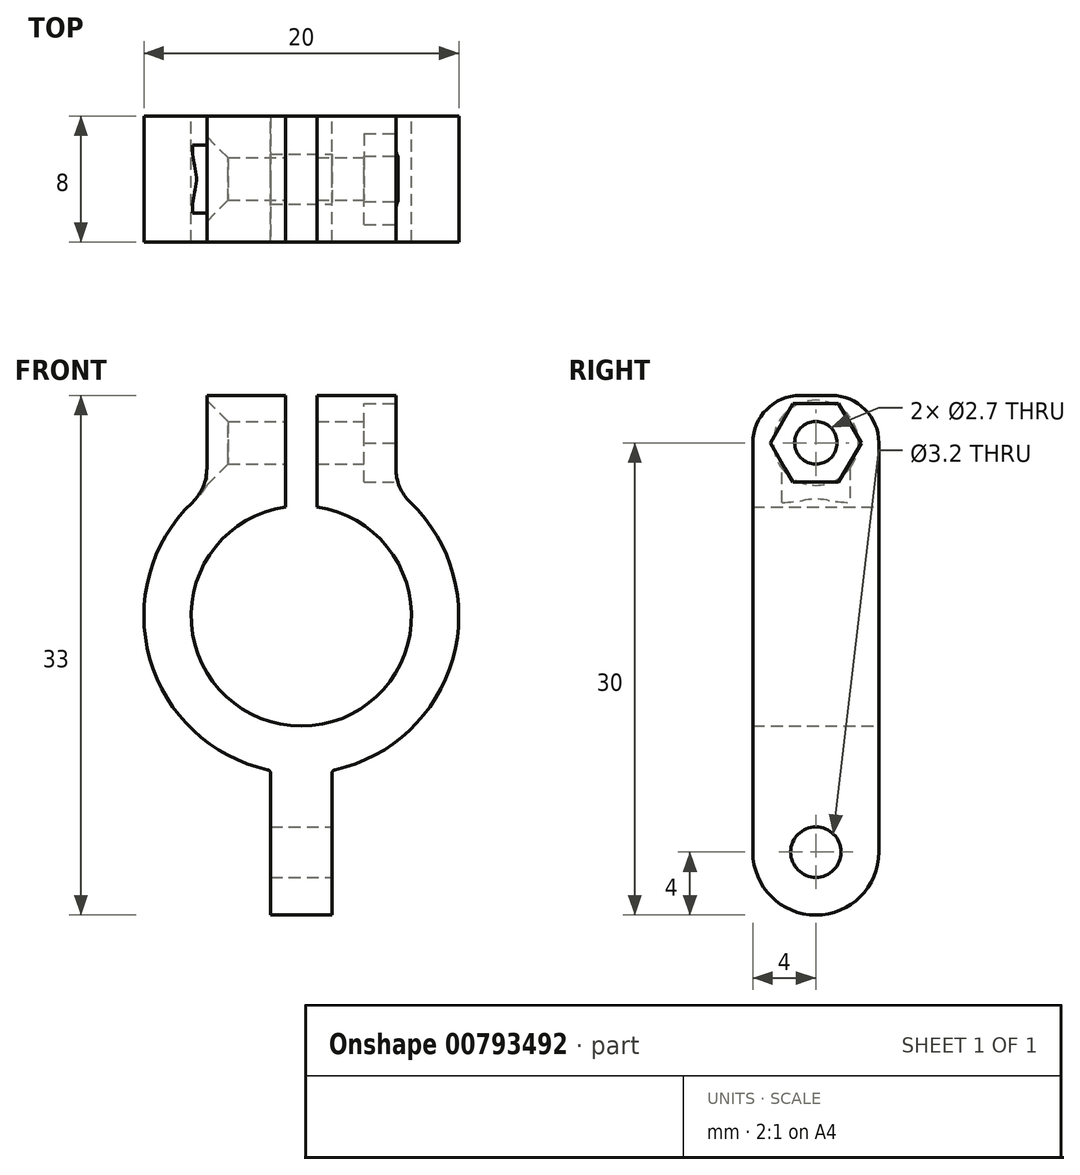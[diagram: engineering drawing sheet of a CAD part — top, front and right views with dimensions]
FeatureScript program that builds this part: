
annotation { "Feature Type Name" : "Feature", "Feature Type Description" : "" }
export const myFeature = defineFeature(function(context is Context, id is Id, definition is map)
    precondition{}
    {
        {
            var Q0;
            Q0=qCreatedBy(makeId("Front.planeOp"),FACE);
            var sketch = newSketch(context, id + "F0", { "sketchPlane" : qUnion([Q0])});
            skArc(sketch, "E0", {"start": v(-1, 6.93) * mm, "mid": v(0, -7) * mm, "end": v(1, 6.93) * mm});
            skLineSegment(sketch, "E1", {"start": v(-1, 14) * mm, "end": v(-1, 6.93) * mm});
            skLineSegment(sketch, "E2", {"start": v(1, 6.93) * mm, "end": v(1, 14) * mm});
            skLineSegment(sketch, "E3.trimOffspring", {"start": v(-1, 14) * mm, "end": v(-6, 14) * mm});
            skLineSegment(sketch, "E4", {"start": v(-1.95, -19) * mm, "end": v(-1.95, -10) * mm});
            skLineSegment(sketch, "E5", {"start": v(1.95, -10) * mm, "end": v(1.95, -19) * mm});
            skLineSegment(sketch, "E6", {"start": v(-1.95, -10) * mm, "end": v(-2.19, -10) * mm, "construction": true});
            skArc(sketch, "E7", {"start": v(-1.95, -10) * mm, "mid": v(-2, -9.85) * mm, "end": v(-2.14, -9.77) * mm});
            skLineSegment(sketch, "E8", {"start": v(-1.95, -19) * mm, "end": v(1.95, -19) * mm});
            skArc(sketch, "E9.MirrorCS", {"start": v(1.95, -10) * mm, "mid": v(2, -9.85) * mm, "end": v(2.14, -9.77) * mm});
            skLineSegment(sketch, "E10", {"start": v(-6, 14) * mm, "end": v(-6, 8) * mm});
            skArc(sketch, "E11", {"start": v(-2.14, -9.77) * mm, "mid": v(-9.77, -2.13) * mm, "end": v(-6, 8) * mm});
            skLineSegment(sketch, "E12.MirrorCS", {"start": v(6, 14) * mm, "end": v(6, 8) * mm});
            skLineSegment(sketch, "E13.MirrorCS", {"start": v(1, 14) * mm, "end": v(6, 14) * mm});
            skArc(sketch, "E14.MirrorCS", {"start": v(2.14, -9.77) * mm, "mid": v(9.77, -2.13) * mm, "end": v(6, 8) * mm});
            skSolve(sketch);
        }
        {
            var Q0;
            Q0=makeQuery(id+"F0.imprint","IMPRINT",FACE,{"disambiguationData":[TD([[makeQuery(id+"F0.imprint","IMPRINT",EDGE,{"derivedFrom":sQuery(id+"F0.wireOp",EDGE,"E0")}),-1.0]])]});
            var Q1;
            {var subQ0=sQuery(id+"F0.wireOp",EDGE,"gT4Yp9KQ-vHPQ-P8ZU-SFqX-VDEBA4EE69W3");Q1=makeQuery(id+"F0.imprint","IMPRINT",FACE,{"disambiguationData":[TD([[makeQuery(id+"F0.imprint","IMPRINT",EDGE,{"derivedFrom":subQ0}),1.0]])]});}
            extrude(context, id + "F1", {"entities" : qUnion([Q0, Q1]), "endBound" : BoundingType.SYMMETRIC, "depth" : 8 * mm, "offsetDistance" : 25 * mm});
        }
        {
            var Q0;
            Q0=makeQuery(id+"F1.opExtrude","SWEPT_FACE",FACE,{"disambiguationData":[OSD([sQuery(id+"F0.wireOp",EDGE,"E12.MirrorCS")])]});
            var sketch = newSketch(context, id + "F2", { "sketchPlane" : qUnion([Q0])});
            skCircle(sketch, "E15", {"center": v(0, 11) * mm, "radius": 1.35 * mm});
            skCircle(sketch, "E16.cCircle", {"center": v(0, 11) * mm, "radius": 2.5 * mm, "construction": true});
            skLineSegment(sketch, "E16.0", {"start": v(-1.44, 13.5) * mm, "end": v(1.44, 13.5) * mm});
            skLineSegment(sketch, "E16.1", {"start": v(1.44, 13.5) * mm, "end": v(2.89, 11) * mm});
            skLineSegment(sketch, "E16.2", {"start": v(2.89, 11) * mm, "end": v(1.44, 8.5) * mm});
            skLineSegment(sketch, "E16.3", {"start": v(1.44, 8.5) * mm, "end": v(-1.44, 8.5) * mm});
            skLineSegment(sketch, "E16.4", {"start": v(-1.44, 8.5) * mm, "end": v(-2.89, 11) * mm});
            skLineSegment(sketch, "E16.5", {"start": v(-2.89, 11) * mm, "end": v(-1.44, 13.5) * mm});
            skPoint(sketch, "E16.0.midPoint", {"position": v(0, 13.5) * mm});
            skSolve(sketch);
        }
        {
            var Q0;
            Q0=makeQuery(id+"F2.imprint","IMPRINT",FACE,{"disambiguationData":[TD([[makeQuery(id+"F2.imprint","IMPRINT",EDGE,{"derivedFrom":sQuery(id+"F2.wireOp",EDGE,"E15")}),1.0]])]});
            var Q1;
            {var subQ0=sQuery(id+"F2.wireOp",EDGE,"nRwaLtps-0aPM-k6Bh-PqO4-CJdIWXvHlXeP");Q1=makeQuery(id+"F2.imprint","IMPRINT",FACE,{"disambiguationData":[TD([[makeQuery(id+"F2.imprint","IMPRINT",EDGE,{"derivedFrom":subQ0}),1.0]])]});}
            var Q2;
            {var subQ0=sQuery(id+"F2.wireOp",EDGE,"26d730cf-6a02-49fb-9eb9-cb2f17dd4a160.MirrorCS");Q2=makeQuery(id+"F2.imprint","IMPRINT",FACE,{"disambiguationData":[TD([[makeQuery(id+"F2.imprint","IMPRINT",EDGE,{"derivedFrom":subQ0}),-1.0]])]});}
            extrude(context, id + "F3", {"entities" : qUnion([Q0, Q1, Q2]), "operationType" : NewBodyOperationType.REMOVE, "oppositeDirection" : true, "depth" : 25 * mm, "offsetDistance" : 25 * mm});
        }
        {
            var Q0;
            Q0=makeQuery(id+"F2.imprint","IMPRINT",FACE,{"disambiguationData":[TD([[makeQuery(id+"F2.imprint","IMPRINT",EDGE,{"derivedFrom":sQuery(id+"F2.wireOp",EDGE,"E15")}),-1.0]])]});
            extrude(context, id + "F4", {"entities" : qUnion([Q0]), "operationType" : NewBodyOperationType.REMOVE, "oppositeDirection" : true, "depth" : 2 * mm, "offsetDistance" : 25 * mm});
        }
        {
            var Q0;
            Q0=makeQuery(id+"F1.opExtrude","SWEPT_FACE",FACE,{"disambiguationData":[OSD([sQuery(id+"F0.wireOp",EDGE,"E5")])]});
            var sketch = newSketch(context, id + "F5", { "sketchPlane" : qUnion([Q0])});
            skCircle(sketch, "E17", {"center": v(0, -15) * mm, "radius": 1.6 * mm});
            skSolve(sketch);
        }
        {
            var Q0;
            Q0=makeQuery(id+"F5.imprint","IMPRINT",FACE,{"disambiguationData":[TD([[makeQuery(id+"F5.imprint","IMPRINT",EDGE,{"derivedFrom":sQuery(id+"F5.wireOp",EDGE,"E17")}),1.0]])]});
            extrude(context, id + "F6", {"entities" : qUnion([Q0]), "operationType" : NewBodyOperationType.REMOVE, "oppositeDirection" : true, "depth" : 25 * mm, "offsetDistance" : 25 * mm});
        }
        {
            var Q0;
            Q0=makeQuery(id+"F3.boolean.opBoolean","INTERSECT",EDGE,{"derivedFrom":[makeQuery(id+"F1.opExtrude","SWEPT_FACE",FACE,{"disambiguationData":[OSD([sQuery(id+"F0.wireOp",EDGE,"E10")])]}),makeQuery(id+"F3.opExtrude","SWEPT_FACE",FACE,{"disambiguationData":[OSD([sQuery(id+"F2.wireOp",EDGE,"E15")])]})]});
            chamfer(context, id + "F7", {"entities" : qUnion([Q0]), "width" : 1.35 * mm, "tangentPropagation" : true});
        }
        {
            var Q0;
            Q0=makeQuery(id+"F1.opExtrude","CAP_EDGE",EDGE,{"disambiguationData":[OSD([sQuery(id+"F0.wireOp",EDGE,"E3.trimOffspring")])],"isStart":false});
            var Q1;
            Q1=makeQuery(id+"F1.opExtrude","CAP_EDGE",EDGE,{"disambiguationData":[OSD([sQuery(id+"F0.wireOp",EDGE,"E3.trimOffspring")])],"isStart":true});
            var Q2;
            Q2=makeQuery(id+"F1.opExtrude","CAP_EDGE",EDGE,{"disambiguationData":[OSD([sQuery(id+"F0.wireOp",EDGE,"E13.MirrorCS")])],"isStart":true});
            var Q3;
            Q3=makeQuery(id+"F1.opExtrude","CAP_EDGE",EDGE,{"disambiguationData":[OSD([sQuery(id+"F0.wireOp",EDGE,"E13.MirrorCS")])],"isStart":false});
            var Q4;
            Q4=makeQuery(id+"F1.opExtrude","SWEPT_EDGE",EDGE,{"disambiguationData":[OSD([sQuery(id+"F0.wireOp",EDGE,"E12.MirrorCS"),sQuery(id+"F0.wireOp",EDGE,"E14.MirrorCS")])]});
            var Q5;
            Q5=makeQuery(id+"F1.opExtrude","SWEPT_EDGE",EDGE,{"disambiguationData":[OSD([sQuery(id+"F0.wireOp",EDGE,"E10"),sQuery(id+"F0.wireOp",EDGE,"E11")])]});
            fillet(context, id + "F8", {"entities" : qUnion([Q0, Q1, Q2, Q3, Q4, Q5]), "radius" : 3 * mm, "tangentPropagation" : true, "allowEdgeOverflow" : false});
        }
        {
            var Q0;
            Q0=makeQuery(id+"F1.opExtrude","CAP_EDGE",EDGE,{"disambiguationData":[OSD([sQuery(id+"F0.wireOp",EDGE,"E8")])],"isStart":false});
            var Q1;
            Q1=makeQuery(id+"F1.opExtrude","CAP_EDGE",EDGE,{"disambiguationData":[OSD([sQuery(id+"F0.wireOp",EDGE,"E8")])],"isStart":true});
            fillet(context, id + "F9", {"entities" : qUnion([Q0, Q1]), "radius" : 4 * mm, "tangentPropagation" : true, "allowEdgeOverflow" : false});
        }
    });
